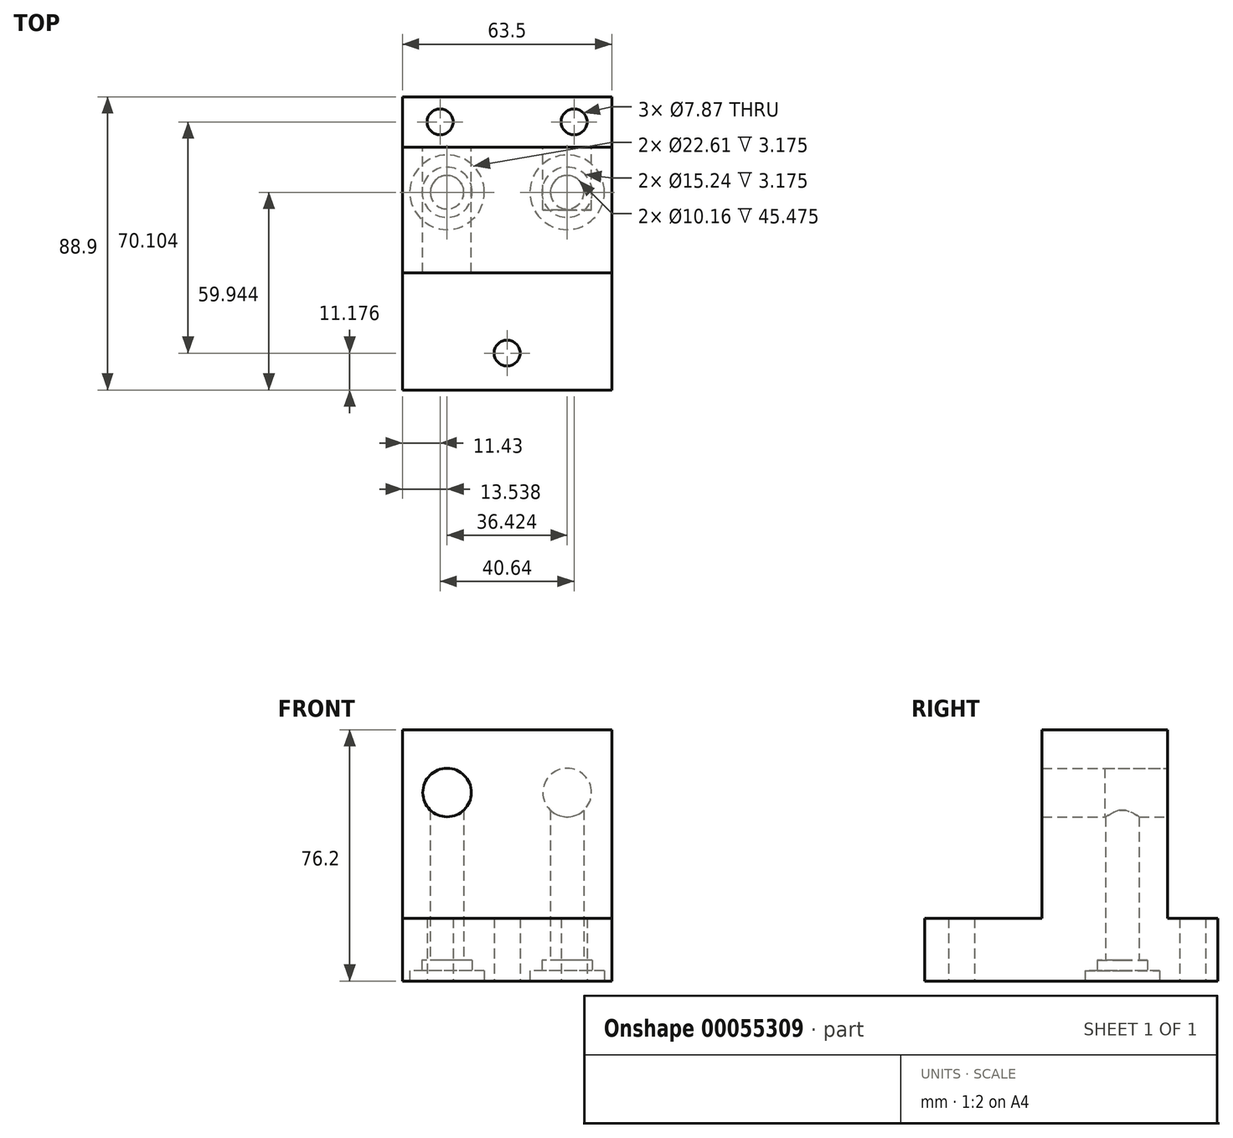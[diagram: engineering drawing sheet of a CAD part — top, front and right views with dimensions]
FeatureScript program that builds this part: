
annotation { "Feature Type Name" : "Feature", "Feature Type Description" : "" }
export const myFeature = defineFeature(function(context is Context, id is Id, definition is map)
    precondition{}
    {
        {
            var Q0;
            Q0=qCreatedBy(makeId("Top.planeOp"),FACE);
            var sketch = newSketch(context, id + "F0", { "sketchPlane" : qUnion([Q0])});
            skLineSegment(sketch, "E0.bottom", {"start": v(0, 0) * mm, "end": v(63.5, 0) * mm});
            skLineSegment(sketch, "E0.top", {"start": v(0, 88.9) * mm, "end": v(63.5, 88.9) * mm});
            skLineSegment(sketch, "E0.left", {"start": v(0, 0) * mm, "end": v(0, 88.9) * mm});
            skLineSegment(sketch, "E0.right", {"start": v(63.5, 0) * mm, "end": v(63.5, 88.9) * mm});
            skCircle(sketch, "E1", {"center": v(11.43, 81.28) * mm, "radius": 3.94 * mm});
            skCircle(sketch, "E2", {"center": v(52.07, 81.28) * mm, "radius": 3.94 * mm});
            skCircle(sketch, "E3", {"center": v(31.75, 11.18) * mm, "radius": 3.94 * mm});
            skCircle(sketch, "E4", {"center": v(13.54, 59.94) * mm, "radius": 7.62 * mm});
            skCircle(sketch, "E5", {"center": v(49.96, 59.94) * mm, "radius": 7.62 * mm});
            skCircle(sketch, "E6", {"center": v(49.96, 59.94) * mm, "radius": 11.3 * mm});
            skCircle(sketch, "E7", {"center": v(13.54, 59.94) * mm, "radius": 11.3 * mm});
            skCircle(sketch, "E8", {"center": v(49.96, 59.94) * mm, "radius": 5.08 * mm});
            skCircle(sketch, "E9", {"center": v(13.54, 59.94) * mm, "radius": 5.08 * mm});
            skLineSegment(sketch, "E10.bottom", {"start": v(63.5, 73.66) * mm, "end": v(0, 73.66) * mm});
            skLineSegment(sketch, "E10.top", {"start": v(63.5, 35.56) * mm, "end": v(0, 35.56) * mm});
            skLineSegment(sketch, "E10.left", {"start": v(63.5, 73.66) * mm, "end": v(63.5, 35.56) * mm});
            skLineSegment(sketch, "E10.right", {"start": v(0, 73.66) * mm, "end": v(0, 35.56) * mm});
            skSolve(sketch);
        }
        {
            var Q0;
            Q0=makeQuery(id+"F0.imprint","IMPRINT",FACE,{"disambiguationData":[TD([[makeQuery(id+"F0.imprint","IMPRINT",EDGE,{"derivedFrom":sQuery(id+"F0.wireOp",EDGE,"E0.bottom")}),1.0]])]});
            var Q1;
            Q1=makeQuery(id+"F0.imprint","IMPRINT",FACE,{"disambiguationData":[TD([[makeQuery(id+"F0.imprint","IMPRINT",EDGE,{"derivedFrom":sQuery(id+"F0.wireOp",EDGE,"E5")}),-1.0]])]});
            var Q2;
            Q2=makeQuery(id+"F0.imprint","IMPRINT",FACE,{"disambiguationData":[TD([[makeQuery(id+"F0.imprint","IMPRINT",EDGE,{"derivedFrom":sQuery(id+"F0.wireOp",EDGE,"E4")}),-1.0]])]});
            var Q3;
            Q3=makeQuery(id+"F0.imprint","IMPRINT",FACE,{"disambiguationData":[TD([[makeQuery(id+"F0.imprint","IMPRINT",EDGE,{"derivedFrom":sQuery(id+"F0.wireOp",EDGE,"E5")}),1.0]])]});
            var Q4;
            Q4=makeQuery(id+"F0.imprint","IMPRINT",FACE,{"disambiguationData":[TD([[makeQuery(id+"F0.imprint","IMPRINT",EDGE,{"derivedFrom":sQuery(id+"F0.wireOp",EDGE,"E4")}),1.0]])]});
            var Q5;
            {var subQ1=sQuery(id+"F0.wireOp",EDGE,"E0.top");Q5=makeQuery(id+"F0.imprint","IMPRINT",FACE,{"disambiguationData":[TD([[makeQuery(id+"F0.imprint","IMPRINT",EDGE,{"derivedFrom":subQ1}),-1.0]])]});}
            var Q6;
            Q6=makeQuery(id+"F0.imprint","IMPRINT",FACE,{"disambiguationData":[TD([[makeQuery(id+"F0.imprint","IMPRINT",EDGE,{"derivedFrom":sQuery(id+"F0.wireOp",EDGE,"E6")}),-1.0]])]});
            var Q7;
            Q7=makeQuery(id+"F0.imprint","IMPRINT",FACE,{"disambiguationData":[TD([[makeQuery(id+"F0.imprint","IMPRINT",EDGE,{"derivedFrom":sQuery(id+"F0.wireOp",EDGE,"E8")}),1.0]])]});
            var Q8;
            Q8=makeQuery(id+"F0.imprint","IMPRINT",FACE,{"disambiguationData":[TD([[makeQuery(id+"F0.imprint","IMPRINT",EDGE,{"derivedFrom":sQuery(id+"F0.wireOp",EDGE,"E9")}),1.0]])]});
            extrude(context, id + "F1", {"entities" : qUnion([Q0, Q1, Q2, Q3, Q4, Q5, Q6, Q7, Q8]), "depth" : 19.05 * mm});
        }
        {
            var Q0;
            Q0=makeQuery(id+"F0.imprint","IMPRINT",FACE,{"disambiguationData":[TD([[makeQuery(id+"F0.imprint","IMPRINT",EDGE,{"derivedFrom":sQuery(id+"F0.wireOp",EDGE,"E6")}),-1.0]])]});
            var Q1;
            Q1=makeQuery(id+"F0.imprint","IMPRINT",FACE,{"disambiguationData":[TD([[makeQuery(id+"F0.imprint","IMPRINT",EDGE,{"derivedFrom":sQuery(id+"F0.wireOp",EDGE,"E4")}),-1.0]])]});
            var Q2;
            Q2=makeQuery(id+"F0.imprint","IMPRINT",FACE,{"disambiguationData":[TD([[makeQuery(id+"F0.imprint","IMPRINT",EDGE,{"derivedFrom":sQuery(id+"F0.wireOp",EDGE,"E5")}),-1.0]])]});
            var Q3;
            Q3=makeQuery(id+"F0.imprint","IMPRINT",FACE,{"disambiguationData":[TD([[makeQuery(id+"F0.imprint","IMPRINT",EDGE,{"derivedFrom":sQuery(id+"F0.wireOp",EDGE,"E5")}),1.0]])]});
            var Q4;
            Q4=makeQuery(id+"F0.imprint","IMPRINT",FACE,{"disambiguationData":[TD([[makeQuery(id+"F0.imprint","IMPRINT",EDGE,{"derivedFrom":sQuery(id+"F0.wireOp",EDGE,"E4")}),1.0]])]});
            var Q5;
            Q5=makeQuery(id+"F0.imprint","IMPRINT",FACE,{"disambiguationData":[TD([[makeQuery(id+"F0.imprint","IMPRINT",EDGE,{"derivedFrom":sQuery(id+"F0.wireOp",EDGE,"E8")}),1.0]])]});
            var Q6;
            Q6=makeQuery(id+"F0.imprint","IMPRINT",FACE,{"disambiguationData":[TD([[makeQuery(id+"F0.imprint","IMPRINT",EDGE,{"derivedFrom":sQuery(id+"F0.wireOp",EDGE,"E9")}),1.0]])]});
            extrude(context, id + "F2", {"entities" : qUnion([Q0, Q1, Q2, Q3, Q4, Q5, Q6]), "operationType" : NewBodyOperationType.ADD, "depth" : 76.2 * mm});
        }
        {
            var Q0;
            Q0=makeQuery(id+"F0.imprint","IMPRINT",FACE,{"disambiguationData":[TD([[makeQuery(id+"F0.imprint","IMPRINT",EDGE,{"derivedFrom":sQuery(id+"F0.wireOp",EDGE,"E5")}),-1.0]])]});
            var Q1;
            Q1=makeQuery(id+"F0.imprint","IMPRINT",FACE,{"disambiguationData":[TD([[makeQuery(id+"F0.imprint","IMPRINT",EDGE,{"derivedFrom":sQuery(id+"F0.wireOp",EDGE,"E4")}),-1.0]])]});
            extrude(context, id + "F3", {"entities" : qUnion([Q0, Q1]), "operationType" : NewBodyOperationType.REMOVE, "depth" : 3.17 * mm});
        }
        {
            var Q0;
            Q0=makeQuery(id+"F0.imprint","IMPRINT",FACE,{"disambiguationData":[TD([[makeQuery(id+"F0.imprint","IMPRINT",EDGE,{"derivedFrom":sQuery(id+"F0.wireOp",EDGE,"E5")}),1.0]])]});
            var Q1;
            Q1=makeQuery(id+"F0.imprint","IMPRINT",FACE,{"disambiguationData":[TD([[makeQuery(id+"F0.imprint","IMPRINT",EDGE,{"derivedFrom":sQuery(id+"F0.wireOp",EDGE,"E4")}),1.0]])]});
            extrude(context, id + "F4", {"entities" : qUnion([Q0, Q1]), "operationType" : NewBodyOperationType.REMOVE, "depth" : 6.35 * mm});
        }
        {
            var Q0;
            Q0=makeQuery(id+"F2.opExtrude","SWEPT_FACE",FACE,{"disambiguationData":[OSD([sQuery(id+"F0.wireOp",EDGE,"E10.bottom")])]});
            var sketch = newSketch(context, id + "F5", { "sketchPlane" : qUnion([Q0])});
            skCircle(sketch, "E11", {"center": v(-13.54, 57.15) * mm, "radius": 7.37 * mm});
            skCircle(sketch, "E12", {"center": v(-49.96, 57.15) * mm, "radius": 7.37 * mm});
            skSolve(sketch);
        }
        {
            var Q0;
            Q0=makeQuery(id+"F5.imprint","IMPRINT",FACE,{"disambiguationData":[TD([[makeQuery(id+"F5.imprint","IMPRINT",EDGE,{"derivedFrom":sQuery(id+"F5.wireOp",EDGE,"E12")}),1.0]])]});
            extrude(context, id + "F6", {"entities" : qUnion([Q0]), "operationType" : NewBodyOperationType.REMOVE, "oppositeDirection" : true, "depth" : 19.05 * mm});
        }
        {
            var Q0;
            Q0=makeQuery(id+"F5.imprint","IMPRINT",FACE,{"disambiguationData":[TD([[makeQuery(id+"F5.imprint","IMPRINT",EDGE,{"derivedFrom":sQuery(id+"F5.wireOp",EDGE,"E11")}),1.0]])]});
            extrude(context, id + "F7", {"entities" : qUnion([Q0]), "operationType" : NewBodyOperationType.REMOVE, "oppositeDirection" : true, "depth" : 50.8 * mm});
        }
        {
            var Q0;
            Q0=makeQuery(id+"F0.imprint","IMPRINT",FACE,{"disambiguationData":[TD([[makeQuery(id+"F0.imprint","IMPRINT",EDGE,{"derivedFrom":sQuery(id+"F0.wireOp",EDGE,"E8")}),1.0]])]});
            var Q1;
            Q1=makeQuery(id+"F0.imprint","IMPRINT",FACE,{"disambiguationData":[TD([[makeQuery(id+"F0.imprint","IMPRINT",EDGE,{"derivedFrom":sQuery(id+"F0.wireOp",EDGE,"E9")}),1.0]])]});
            extrude(context, id + "F8", {"entities" : qUnion([Q0, Q1]), "operationType" : NewBodyOperationType.REMOVE, "depth" : 57.15 * mm});
        }
    });
